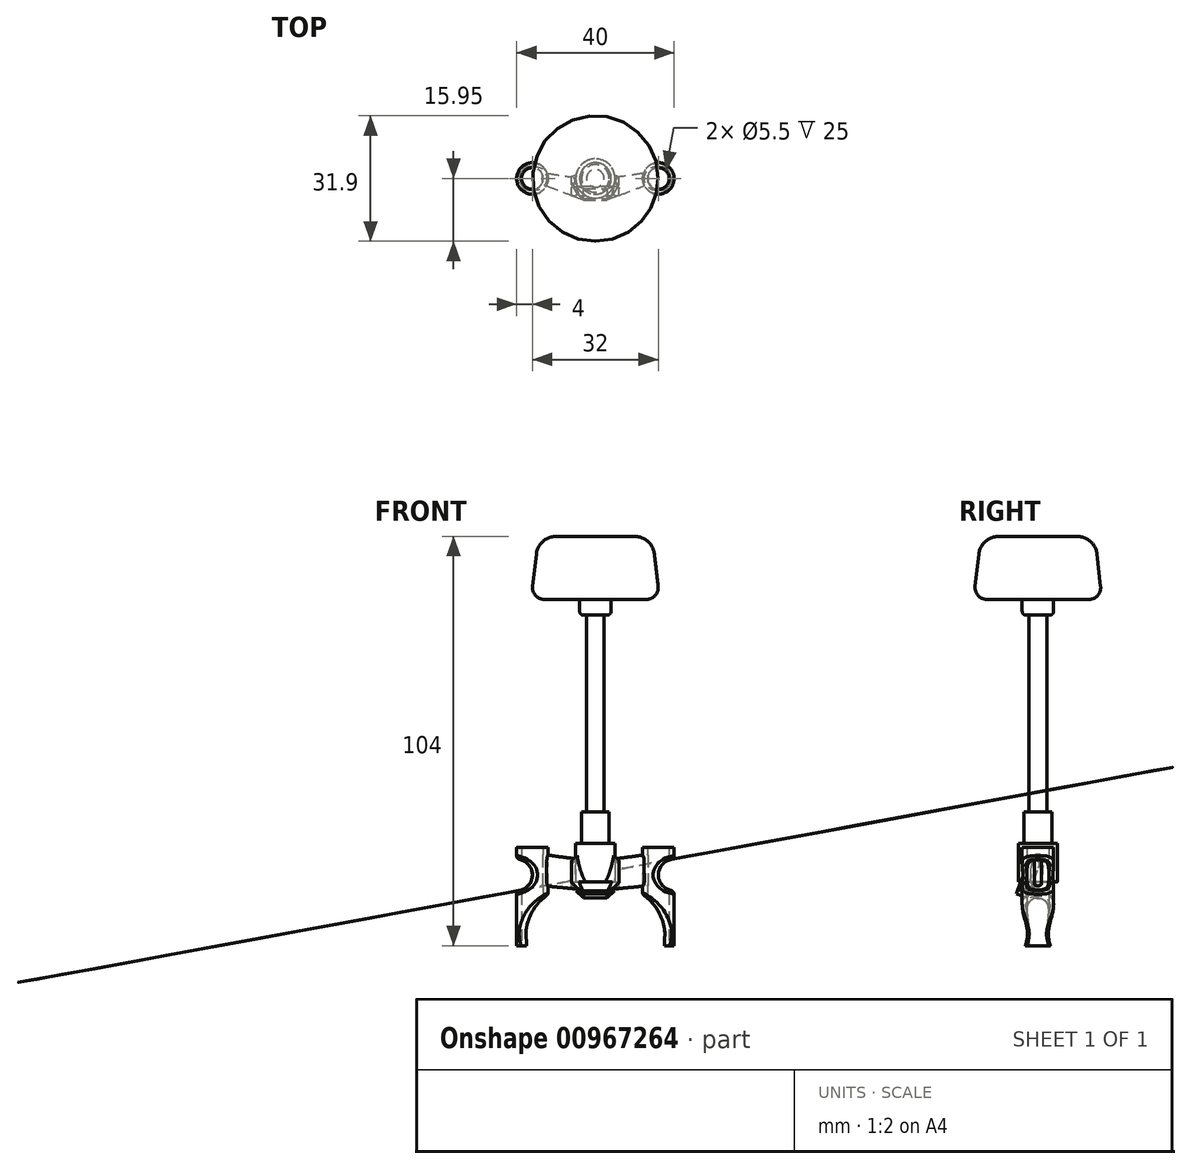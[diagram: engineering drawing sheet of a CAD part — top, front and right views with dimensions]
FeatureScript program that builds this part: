
annotation { "Feature Type Name" : "Feature", "Feature Type Description" : "" }
export const myFeature = defineFeature(function(context is Context, id is Id, definition is map)
    precondition{}
    {
        {
            var Q0;
            Q0=qCreatedBy(makeId("Top.planeOp"),FACE);
            var sketch = newSketch(context, id + "F0", { "sketchPlane" : qUnion([Q0])});
            skCircle(sketch, "E0", {"center": v(-16, 0) * mm, "radius": 2.75 * mm});
            skCircle(sketch, "E1", {"center": v(16, 0) * mm, "radius": 2.75 * mm});
            skCircle(sketch, "E2", {"center": v(-16, 0) * mm, "radius": 4 * mm});
            skCircle(sketch, "E3", {"center": v(16, 0) * mm, "radius": 4 * mm});
            skSolve(sketch);
        }
        {
            var Q0;
            Q0=qSketchRegion(id+"F0",true);
            extrude(context, id + "F1", {"entities" : qUnion([Q0]), "depth" : 11 * mm});
        }
        {
            var Q0;
            Q0=qCreatedBy(makeId("Right.planeOp"),FACE);
            var sketch = newSketch(context, id + "F2", { "sketchPlane" : qUnion([Q0])});
            skLineSegment(sketch, "E4.bottom", {"start": v(-5.42, -0.75) * mm, "end": v(-2.6, -1.78) * mm});
            skLineSegment(sketch, "E4.top", {"start": v(-1.32, 10.53) * mm, "end": v(1.5, 9.5) * mm});
            skLineSegment(sketch, "E4.left", {"start": v(-5.42, -0.75) * mm, "end": v(-1.32, 10.53) * mm});
            skLineSegment(sketch, "E4.right", {"start": v(-2.6, -1.78) * mm, "end": v(1.5, 9.5) * mm});
            skPoint(sketch, "E4.middle", {"position": v(-1.96, 4.37) * mm});
            skSolve(sketch);
        }
        {
            var Q0;
            Q0=qSketchRegion(id+"F2",true);
            var Q1;
            Q1=makeQuery(id+"F1.opExtrude","SWEPT_FACE",FACE,{"disambiguationData":[OSD([sQuery(id+"F0.wireOp",EDGE,"E3")])]});
            var Q2;
            Q2=makeQuery(id+"F1.opExtrude","SWEPT_BODY",BODY,{"disambiguationData":[OSD([sQuery(id+"F0.wireOp",EDGE,"E1"),sQuery(id+"F0.wireOp",EDGE,"E3")])]});
            extrude(context, id + "F3", {"entities" : qUnion([Q0]), "operationType" : NewBodyOperationType.ADD, "endBound" : BoundingType.SYMMETRIC, "oppositeDirection" : true, "endBoundEntityFace" : qUnion([Q1]), "endBoundEntityBody" : qUnion([Q2]), "depth" : 12 * mm});
        }
        {
            var Q0;
            Q0=qCreatedBy(makeId("Right.planeOp"),FACE);
            cPlane(context, id + "F4", {"entities" : qUnion([Q0]), "cplaneType" : CPlaneType.OFFSET, "offset" : (16 - 2.6) * mm, "oppositeDirection" : true, "width" : 150 * mm, "height" : 150 * mm});
        }
        {
            var Q0;
            Q0=qCreatedBy(id+"F4.planeOp",FACE);
            var sketch = newSketch(context, id + "F5", { "sketchPlane" : qUnion([Q0])});
            skLineSegment(sketch, "E5.bottom", {"start": v(0, 1.25) * mm, "end": v(0, 1.25) * mm});
            skLineSegment(sketch, "E5.top", {"start": v(0, 9.25) * mm, "end": v(0, 9.25) * mm});
            skLineSegment(sketch, "E5.left", {"start": v(1.5, 2.75) * mm, "end": v(1.5, 7.75) * mm});
            skLineSegment(sketch, "E5.right", {"start": v(-1.5, 2.75) * mm, "end": v(-1.5, 7.75) * mm});
            skPoint(sketch, "E5.middle", {"position": v(0, 5.25) * mm});
            skPoint(sketch, "E6.visualSharp", {"position": v(-1.5, 9.25) * mm});
            skArc(sketch, "E6.filletArc", {"start": v(0, 9.25) * mm, "mid": v(-1.06, 8.81) * mm, "end": v(-1.5, 7.75) * mm});
            skPoint(sketch, "E7.visualSharp", {"position": v(1.5, 9.25) * mm});
            skArc(sketch, "E7.filletArc", {"start": v(1.5, 7.75) * mm, "mid": v(1.06, 8.81) * mm, "end": v(0, 9.25) * mm});
            skPoint(sketch, "E8.visualSharp", {"position": v(-1.5, 1.25) * mm});
            skArc(sketch, "E8.filletArc", {"start": v(-1.5, 2.75) * mm, "mid": v(-1.06, 1.69) * mm, "end": v(0, 1.25) * mm});
            skPoint(sketch, "E9.visualSharp", {"position": v(1.5, 1.25) * mm});
            skArc(sketch, "E9.filletArc", {"start": v(0, 1.25) * mm, "mid": v(1.06, 1.69) * mm, "end": v(1.5, 2.75) * mm});
            skSolve(sketch);
        }
        {
            var Q0;
            Q0=makeQuery(id+"F3.opExtrude","CAP_FACE",FACE,{"disambiguationData":[OSD([sQuery(id+"F2.wireOp",EDGE,"E4.bottom"),sQuery(id+"F2.wireOp",EDGE,"E4.top"),sQuery(id+"F2.wireOp",EDGE,"E4.left"),sQuery(id+"F2.wireOp",EDGE,"E4.right")])],"isStart":false});
            var sketch = newSketch(context, id + "F6", { "sketchPlane" : qUnion([Q0])});
            skLineSegment(sketch, "E10", {"start": v(0.6, 8.13) * mm, "end": v(0.6, 8.13) * mm});
            skLineSegment(sketch, "E11", {"start": v(2.52, 7.24) * mm, "end": v(4.23, 2.54) * mm});
            skLineSegment(sketch, "E12", {"start": v(3.33, 0.62) * mm, "end": v(3.33, 0.62) * mm});
            skLineSegment(sketch, "E13", {"start": v(1.4, 1.51) * mm, "end": v(-0.3, 6.21) * mm});
            skPoint(sketch, "E14.visualSharp", {"position": v(-0.82, 7.62) * mm});
            skArc(sketch, "E14.filletArc", {"start": v(0.6, 8.13) * mm, "mid": v(-0.25, 7.36) * mm, "end": v(-0.3, 6.21) * mm});
            skPoint(sketch, "E15.visualSharp", {"position": v(2, 8.65) * mm});
            skArc(sketch, "E15.filletArc", {"start": v(2.52, 7.24) * mm, "mid": v(1.74, 8.08) * mm, "end": v(0.6, 8.13) * mm});
            skPoint(sketch, "E16.visualSharp", {"position": v(4.74, 1.13) * mm});
            skArc(sketch, "E16.filletArc", {"start": v(3.33, 0.62) * mm, "mid": v(4.18, 1.4) * mm, "end": v(4.23, 2.54) * mm});
            skPoint(sketch, "E17.visualSharp", {"position": v(1.92, 0.1) * mm});
            skArc(sketch, "E17.filletArc", {"start": v(1.4, 1.51) * mm, "mid": v(2.18, 0.67) * mm, "end": v(3.33, 0.62) * mm});
            skSolve(sketch);
        }
        {
            var Q2;
            Q2=qSketchRegion(id+"F6",true);
            var Q3;
            Q3=qSketchRegion(id+"F5",true);
            loft(context, id + "F7", {"operationType" : NewBodyOperationType.ADD, "sheetProfilesArray" : [{ "sheetProfileEntities" : qUnion([Q2]) }, { "sheetProfileEntities" : qUnion([Q3]) }]});
        }
        {
            var Q0;
            Q0=makeQuery(id+"F3.opExtrude","CAP_FACE",FACE,{"disambiguationData":[OSD([sQuery(id+"F2.wireOp",EDGE,"E4.bottom"),sQuery(id+"F2.wireOp",EDGE,"E4.top"),sQuery(id+"F2.wireOp",EDGE,"E4.left"),sQuery(id+"F2.wireOp",EDGE,"E4.right")])],"isStart":true});
            var sketch = newSketch(context, id + "F8", { "sketchPlane" : qUnion([Q0])});
            skLineSegment(sketch, "E18", {"start": v(-0.6, 8.13) * mm, "end": v(-0.6, 8.13) * mm});
            skLineSegment(sketch, "E19", {"start": v(0.3, 6.21) * mm, "end": v(-1.4, 1.51) * mm});
            skLineSegment(sketch, "E20", {"start": v(-3.33, 0.62) * mm, "end": v(-3.33, 0.62) * mm});
            skLineSegment(sketch, "E21", {"start": v(-4.23, 2.54) * mm, "end": v(-2.52, 7.24) * mm});
            skPoint(sketch, "E22.visualSharp", {"position": v(-2, 8.65) * mm});
            skArc(sketch, "E22.filletArc", {"start": v(-0.6, 8.13) * mm, "mid": v(-1.74, 8.08) * mm, "end": v(-2.52, 7.24) * mm});
            skPoint(sketch, "E23.visualSharp", {"position": v(0.82, 7.62) * mm});
            skArc(sketch, "E23.filletArc", {"start": v(0.3, 6.21) * mm, "mid": v(0.25, 7.36) * mm, "end": v(-0.6, 8.13) * mm});
            skPoint(sketch, "E24.visualSharp", {"position": v(-4.74, 1.13) * mm});
            skArc(sketch, "E24.filletArc", {"start": v(-4.23, 2.54) * mm, "mid": v(-4.18, 1.4) * mm, "end": v(-3.33, 0.62) * mm});
            skPoint(sketch, "E25.visualSharp", {"position": v(-1.92, 0.1) * mm});
            skArc(sketch, "E25.filletArc", {"start": v(-3.33, 0.62) * mm, "mid": v(-2.18, 0.67) * mm, "end": v(-1.4, 1.51) * mm});
            skSolve(sketch);
        }
        {
            var Q0;
            Q0=qCreatedBy(makeId("Right.planeOp"),FACE);
            cPlane(context, id + "F9", {"entities" : qUnion([Q0]), "cplaneType" : CPlaneType.OFFSET, "offset" : 13.4 * mm, "width" : 150 * mm, "height" : 150 * mm});
        }
        {
            var Q0;
            Q0=qCreatedBy(id+"F9.planeOp",FACE);
            var sketch = newSketch(context, id + "F10", { "sketchPlane" : qUnion([Q0])});
            skLineSegment(sketch, "E26.bottom", {"start": v(0, 9.25) * mm, "end": v(0, 9.25) * mm});
            skLineSegment(sketch, "E26.top", {"start": v(0, 1.25) * mm, "end": v(0, 1.25) * mm});
            skLineSegment(sketch, "E26.left", {"start": v(-1.5, 7.75) * mm, "end": v(-1.5, 2.75) * mm});
            skLineSegment(sketch, "E26.right", {"start": v(1.5, 7.75) * mm, "end": v(1.5, 2.75) * mm});
            skPoint(sketch, "E27.visualSharp", {"position": v(-1.5, 9.25) * mm});
            skArc(sketch, "E27.filletArc", {"start": v(0, 9.25) * mm, "mid": v(-1.06, 8.81) * mm, "end": v(-1.5, 7.75) * mm});
            skPoint(sketch, "E28.visualSharp", {"position": v(1.5, 9.25) * mm});
            skArc(sketch, "E28.filletArc", {"start": v(1.5, 7.75) * mm, "mid": v(1.06, 8.81) * mm, "end": v(0, 9.25) * mm});
            skPoint(sketch, "E29.visualSharp", {"position": v(-1.5, 1.25) * mm});
            skArc(sketch, "E29.filletArc", {"start": v(-1.5, 2.75) * mm, "mid": v(-1.06, 1.69) * mm, "end": v(0, 1.25) * mm});
            skPoint(sketch, "E30.visualSharp", {"position": v(1.5, 1.25) * mm});
            skArc(sketch, "E30.filletArc", {"start": v(0, 1.25) * mm, "mid": v(1.06, 1.69) * mm, "end": v(1.5, 2.75) * mm});
            skSolve(sketch);
        }
        {
            var Q2;
            Q2=qSketchRegion(id+"F8",true);
            var Q3;
            Q3=qSketchRegion(id+"F10",true);
            loft(context, id + "F11", {"operationType" : NewBodyOperationType.ADD, "sheetProfilesArray" : [{ "sheetProfileEntities" : qUnion([Q2]) }, { "sheetProfileEntities" : qUnion([Q3]) }]});
        }
        {
            var Q0;
            Q0=makeQuery(id+"F3.opExtrude","SWEPT_FACE",FACE,{"disambiguationData":[OSD([sQuery(id+"F2.wireOp",EDGE,"E4.left")])]});
            var sketch = newSketch(context, id + "F12", { "sketchPlane" : qUnion([Q0])});
            skCircle(sketch, "E31", {"center": v(0, 3.44) * mm, "radius": 3.5 * mm});
            skSolve(sketch);
        }
        {
            var Q0;
            Q0=makeQuery(id+"F12.imprint","IMPRINT",FACE,{"disambiguationData":[TD([[makeQuery(id+"F12.imprint","IMPRINT",EDGE,{"derivedFrom":sQuery(id+"F12.wireOp",EDGE,"E31")}),1.0]])]});
            extrude(context, id + "F13", {"entities" : qUnion([Q0]), "operationType" : NewBodyOperationType.REMOVE, "oppositeDirection" : true, "depth" : 25 * mm});
        }
        {
            var Q0;
            Q0=makeQuery(id+"F3.opExtrude","CAP_EDGE",EDGE,{"disambiguationData":[OSD([sQuery(id+"F2.wireOp",EDGE,"E4.top")])],"isStart":false});
            var Q1;
            Q1=makeQuery(id+"F3.opExtrude","CAP_EDGE",EDGE,{"disambiguationData":[OSD([sQuery(id+"F2.wireOp",EDGE,"E4.top")])],"isStart":true});
            var Q2;
            Q2=makeQuery(id+"F3.opExtrude","CAP_EDGE",EDGE,{"disambiguationData":[OSD([sQuery(id+"F2.wireOp",EDGE,"E4.bottom")])],"isStart":true});
            var Q3;
            Q3=makeQuery(id+"F3.opExtrude","CAP_EDGE",EDGE,{"disambiguationData":[OSD([sQuery(id+"F2.wireOp",EDGE,"E4.bottom")])],"isStart":false});
            chamfer(context, id + "F14", {"entities" : qUnion([Q0, Q1, Q2, Q3]), "width" : 3 * mm, "tangentPropagation" : true});
        }
        {
            var Q0;
            Q0=qCreatedBy(makeId("Top.planeOp"),FACE);
            var sketch = newSketch(context, id + "F15", { "sketchPlane" : qUnion([Q0])});
            skCircle(sketch, "E32", {"center": v(0, 0) * mm, "radius": 3.5 * mm});
            skSolve(sketch);
        }
        {
            var Q0;
            Q0=makeQuery(id+"F15.imprint","IMPRINT",FACE,{"disambiguationData":[TD([[makeQuery(id+"F15.imprint","IMPRINT",EDGE,{"derivedFrom":sQuery(id+"F15.wireOp",EDGE,"E32")}),1.0]])]});
            extrude(context, id + "F16", {"entities" : qUnion([Q0]), "depth" : 20 * mm});
        }
        {
            var Q0;
            Q0=makeQuery(id+"F1.opExtrude","CAP_FACE",FACE,{"disambiguationData":[OSD([sQuery(id+"F0.wireOp",EDGE,"E0"),sQuery(id+"F0.wireOp",EDGE,"E2")])],"isStart":true});
            var Q1;
            Q1=makeQuery(id+"F1.opExtrude","CAP_FACE",FACE,{"disambiguationData":[OSD([sQuery(id+"F0.wireOp",EDGE,"E1"),sQuery(id+"F0.wireOp",EDGE,"E3")])],"isStart":true});
            extrude(context, id + "F17", {"entities" : qUnion([Q0, Q1]), "operationType" : NewBodyOperationType.ADD, "depth" : 14 * mm});
        }
        {
            var Q0;
            Q0=qCreatedBy(makeId("Front.planeOp"),FACE);
            var sketch = newSketch(context, id + "F18", { "sketchPlane" : qUnion([Q0])});
            skLineSegment(sketch, "E33", {"start": v(-17.5, -14) * mm, "end": v(-17.5, -11) * mm});
            skArc(sketch, "E34", {"start": v(-12, -1) * mm, "mid": v(-16.03, -5.3) * mm, "end": v(-17.5, -11) * mm});
            skLineSegment(sketch, "E35", {"start": v(-12, -1) * mm, "end": v(-12, -14) * mm});
            skLineSegment(sketch, "E36", {"start": v(-12, -14) * mm, "end": v(-17.5, -14) * mm});
            skPoint(sketch, "E37.orphan", {"position": v(-12, 0) * mm});
            skArc(sketch, "E38.MirrorCS", {"start": v(12, -1) * mm, "mid": v(16.03, -5.3) * mm, "end": v(17.5, -11) * mm});
            skPoint(sketch, "E39.MirrorP", {"position": v(12, 0) * mm});
            skLineSegment(sketch, "E40.MirrorCS", {"start": v(12, -1) * mm, "end": v(12, -14) * mm});
            skLineSegment(sketch, "E41.MirrorCS", {"start": v(17.5, -14) * mm, "end": v(17.5, -11) * mm});
            skLineSegment(sketch, "E42.MirrorCS", {"start": v(12, -14) * mm, "end": v(17.5, -14) * mm});
            skCircle(sketch, "E43", {"center": v(-20, 4) * mm, "radius": 4 * mm});
            skCircle(sketch, "E44.MirrorC", {"center": v(20, 4) * mm, "radius": 4 * mm});
            skSolve(sketch);
        }
        {
            var Q0;
            Q0=qSketchRegion(id+"F18",true);
            extrude(context, id + "F19", {"entities" : qUnion([Q0]), "operationType" : NewBodyOperationType.REMOVE, "endBound" : BoundingType.SYMMETRIC, "oppositeDirection" : true, "depth" : 25 * mm});
        }
        {
            var Q0;
            {var subQ0=sQuery(id+"F0.wireOp",EDGE,"E2");Q0=makeQuery(id+"F19.boolean.opBoolean","INTERSECT",EDGE,{"disambiguationData":[OD(0.0)],"derivedFrom":[makeQuery(id+"F17.boolean.opBoolean","MERGE",FACE,{"derivedFrom":[makeQuery(id+"F1.opExtrude","SWEPT_FACE",FACE,{"disambiguationData":[OSD([subQ0])]}),makeQuery(id+"F17.opExtrude","SWEPT_FACE",FACE,{"disambiguationData":[OSD([subQ0])]})]}),makeQuery(id+"F19.opExtrude","SWEPT_FACE",FACE,{"disambiguationData":[OSD([sQuery(id+"F18.wireOp",EDGE,"E33")])]})]});}
            var Q1;
            {var subQ0=sQuery(id+"F0.wireOp",EDGE,"E2");Q1=makeQuery(id+"F19.boolean.opBoolean","INTERSECT",EDGE,{"derivedFrom":[makeQuery(id+"F17.boolean.opBoolean","MERGE",FACE,{"derivedFrom":[makeQuery(id+"F1.opExtrude","SWEPT_FACE",FACE,{"disambiguationData":[OSD([subQ0])]}),makeQuery(id+"F17.opExtrude","SWEPT_FACE",FACE,{"disambiguationData":[OSD([subQ0])]})]}),makeQuery(id+"F19.opExtrude","SWEPT_FACE",FACE,{"disambiguationData":[OSD([sQuery(id+"F18.wireOp",EDGE,"E34")])]})]});}
            var Q2;
            {var subQ0=sQuery(id+"F0.wireOp",EDGE,"E3");Q2=makeQuery(id+"F19.boolean.opBoolean","INTERSECT",EDGE,{"disambiguationData":[OD(0.0)],"derivedFrom":[makeQuery(id+"F17.boolean.opBoolean","MERGE",FACE,{"derivedFrom":[makeQuery(id+"F1.opExtrude","SWEPT_FACE",FACE,{"disambiguationData":[OSD([subQ0])]}),makeQuery(id+"F17.opExtrude","SWEPT_FACE",FACE,{"disambiguationData":[OSD([subQ0])]})]}),makeQuery(id+"F19.opExtrude","SWEPT_FACE",FACE,{"disambiguationData":[OSD([sQuery(id+"F18.wireOp",EDGE,"E41.MirrorCS")])]})]});}
            var Q3;
            {var subQ0=sQuery(id+"F0.wireOp",EDGE,"E3");Q3=makeQuery(id+"F19.boolean.opBoolean","INTERSECT",EDGE,{"derivedFrom":[makeQuery(id+"F17.boolean.opBoolean","MERGE",FACE,{"derivedFrom":[makeQuery(id+"F1.opExtrude","SWEPT_FACE",FACE,{"disambiguationData":[OSD([subQ0])]}),makeQuery(id+"F17.opExtrude","SWEPT_FACE",FACE,{"disambiguationData":[OSD([subQ0])]})]}),makeQuery(id+"F19.opExtrude","SWEPT_FACE",FACE,{"disambiguationData":[OSD([sQuery(id+"F18.wireOp",EDGE,"E38.MirrorCS")])]})]});}
            fillet(context, id + "F20", {"entities" : qUnion([Q0, Q1, Q2, Q3]), "radius" : 1 * mm, "tangentPropagation" : true, "allowEdgeOverflow" : false});
        }
        {
            var Q0;
            {var subQ0=sQuery(id+"F0.wireOp",EDGE,"E2");Q0=makeQuery(id+"F19.boolean.opBoolean","INTERSECT",EDGE,{"derivedFrom":[makeQuery(id+"F17.boolean.opBoolean","MERGE",FACE,{"derivedFrom":[makeQuery(id+"F1.opExtrude","SWEPT_FACE",FACE,{"disambiguationData":[OSD([subQ0])]}),makeQuery(id+"F17.opExtrude","SWEPT_FACE",FACE,{"disambiguationData":[OSD([subQ0])]})]}),makeQuery(id+"F19.opExtrude","SWEPT_FACE",FACE,{"disambiguationData":[OSD([sQuery(id+"F18.wireOp",EDGE,"E43")])]})]});}
            var Q1;
            {var subQ0=sQuery(id+"F0.wireOp",EDGE,"E3");Q1=makeQuery(id+"F19.boolean.opBoolean","INTERSECT",EDGE,{"derivedFrom":[makeQuery(id+"F17.boolean.opBoolean","MERGE",FACE,{"derivedFrom":[makeQuery(id+"F1.opExtrude","SWEPT_FACE",FACE,{"disambiguationData":[OSD([subQ0])]}),makeQuery(id+"F17.opExtrude","SWEPT_FACE",FACE,{"disambiguationData":[OSD([subQ0])]})]}),makeQuery(id+"F19.opExtrude","SWEPT_FACE",FACE,{"disambiguationData":[OSD([sQuery(id+"F18.wireOp",EDGE,"E44.MirrorC")])]})]});}
            fillet(context, id + "F21", {"entities" : qUnion([Q0, Q1]), "radius" : 1 * mm, "tangentPropagation" : true, "allowEdgeOverflow" : false});
        }
        {
            var Q0;
            Q0=qCreatedBy(makeId("Top.planeOp"),FACE);
            var sketch = newSketch(context, id + "F22", { "sketchPlane" : qUnion([Q0])});
            skCircle(sketch, "E45", {"center": v(0, 0) * mm, "radius": 5 * mm});
            skSolve(sketch);
        }
        {
            var Q0;
            Q0=qSketchRegion(id+"F22",true);
            extrude(context, id + "F23", {"entities" : qUnion([Q0]), "operationType" : NewBodyOperationType.ADD, "depth" : 12 * mm});
        }
        {
            var Q0;
            Q0=makeQuery(id+"F16.opExtrude","CAP_FACE",FACE,{"disambiguationData":[OSD([sQuery(id+"F15.wireOp",EDGE,"E32")])],"isStart":false});
            var sketch = newSketch(context, id + "F24", { "sketchPlane" : qUnion([Q0])});
            skCircle(sketch, "E46", {"center": v(0, 0) * mm, "radius": 2.25 * mm});
            skSolve(sketch);
        }
        {
            var Q0;
            Q0=makeQuery(id+"F24.imprint","IMPRINT",FACE,{"disambiguationData":[TD([[makeQuery(id+"F24.imprint","IMPRINT",EDGE,{"derivedFrom":sQuery(id+"F24.wireOp",EDGE,"E46")}),1.0]])]});
            extrude(context, id + "F25", {"entities" : qUnion([Q0]), "operationType" : NewBodyOperationType.ADD, "depth" : 55 * mm});
        }
        {
            var Q0;
            Q0=qCreatedBy(makeId("Front.planeOp"),FACE);
            var sketch = newSketch(context, id + "F26", { "sketchPlane" : qUnion([Q0])});
            skLineSegment(sketch, "E47", {"start": v(0, 90) * mm, "end": v(10.03, 90) * mm});
            skLineSegment(sketch, "E48", {"start": v(0, 70) * mm, "end": v(3, 70) * mm});
            skLineSegment(sketch, "E49", {"start": v(0, 70) * mm, "end": v(0, 90) * mm, "construction": true});
            skLineSegment(sketch, "E50", {"start": v(4, 71) * mm, "end": v(4, 73.5) * mm});
            skLineSegment(sketch, "E51", {"start": v(4.5, 74) * mm, "end": v(12.95, 74) * mm});
            skArc(sketch, "E52.filletArc", {"start": v(12.95, 74) * mm, "mid": v(15.2, 75) * mm, "end": v(15.93, 77.34) * mm});
            skLineSegment(sketch, "E53", {"start": v(15.93, 77.34) * mm, "end": v(15, 85.56) * mm});
            skPoint(sketch, "E54.visualSharp", {"position": v(14.5, 90) * mm});
            skArc(sketch, "E54.filletArc", {"start": v(15, 85.56) * mm, "mid": v(13.37, 88.73) * mm, "end": v(10.03, 90) * mm});
            skLineSegment(sketch, "E55", {"start": v(0, 90) * mm, "end": v(0, 70) * mm});
            skPoint(sketch, "E56.visualSharp", {"position": v(4, 70) * mm});
            skArc(sketch, "E56.filletArc", {"start": v(3, 70) * mm, "mid": v(3.7, 70.3) * mm, "end": v(4, 71) * mm});
            skPoint(sketch, "E57.visualSharp", {"position": v(4, 74) * mm});
            skArc(sketch, "E57.filletArc", {"start": v(4.5, 74) * mm, "mid": v(4.15, 73.85) * mm, "end": v(4, 73.5) * mm});
            skSolve(sketch);
        }
        {
            var Q0;
            Q0=makeQuery(id+"F26.imprint","IMPRINT",FACE,{"disambiguationData":[TD([[makeQuery(id+"F26.imprint","IMPRINT",EDGE,{"derivedFrom":sQuery(id+"F26.wireOp",EDGE,"E47")}),-1.0]])]});
            var Q1;
            Q1=sQuery(id+"F26.wireOp",EDGE,"E55");
            revolve(context, id + "F27", {"operationType" : NewBodyOperationType.ADD, "entities" : qUnion([Q0]), "axis" : qUnion([Q1]), "revolveType" : RevolveType.FULL});
        }
        {
            var Q0;
            Q0=qCreatedBy(makeId("Top.planeOp"),FACE);
            var sketch = newSketch(context, id + "F28", { "sketchPlane" : qUnion([Q0])});
            skCircle(sketch, "E58", {"center": v(0, 0) * mm, "radius": 6 * mm});
            skCircle(sketch, "E59", {"center": v(0, 0) * mm, "radius": 4 * mm});
            skSolve(sketch);
        }
        {
            var Q0;
            Q0=makeQuery(id+"F28.imprint","IMPRINT",FACE,{"disambiguationData":[TD([[makeQuery(id+"F28.imprint","IMPRINT",EDGE,{"derivedFrom":sQuery(id+"F28.wireOp",EDGE,"E58")}),1.0]])]});
            extrude(context, id + "F29", {"entities" : qUnion([Q0]), "operationType" : NewBodyOperationType.REMOVE, "depth" : 2.3 * mm});
        }
    });
